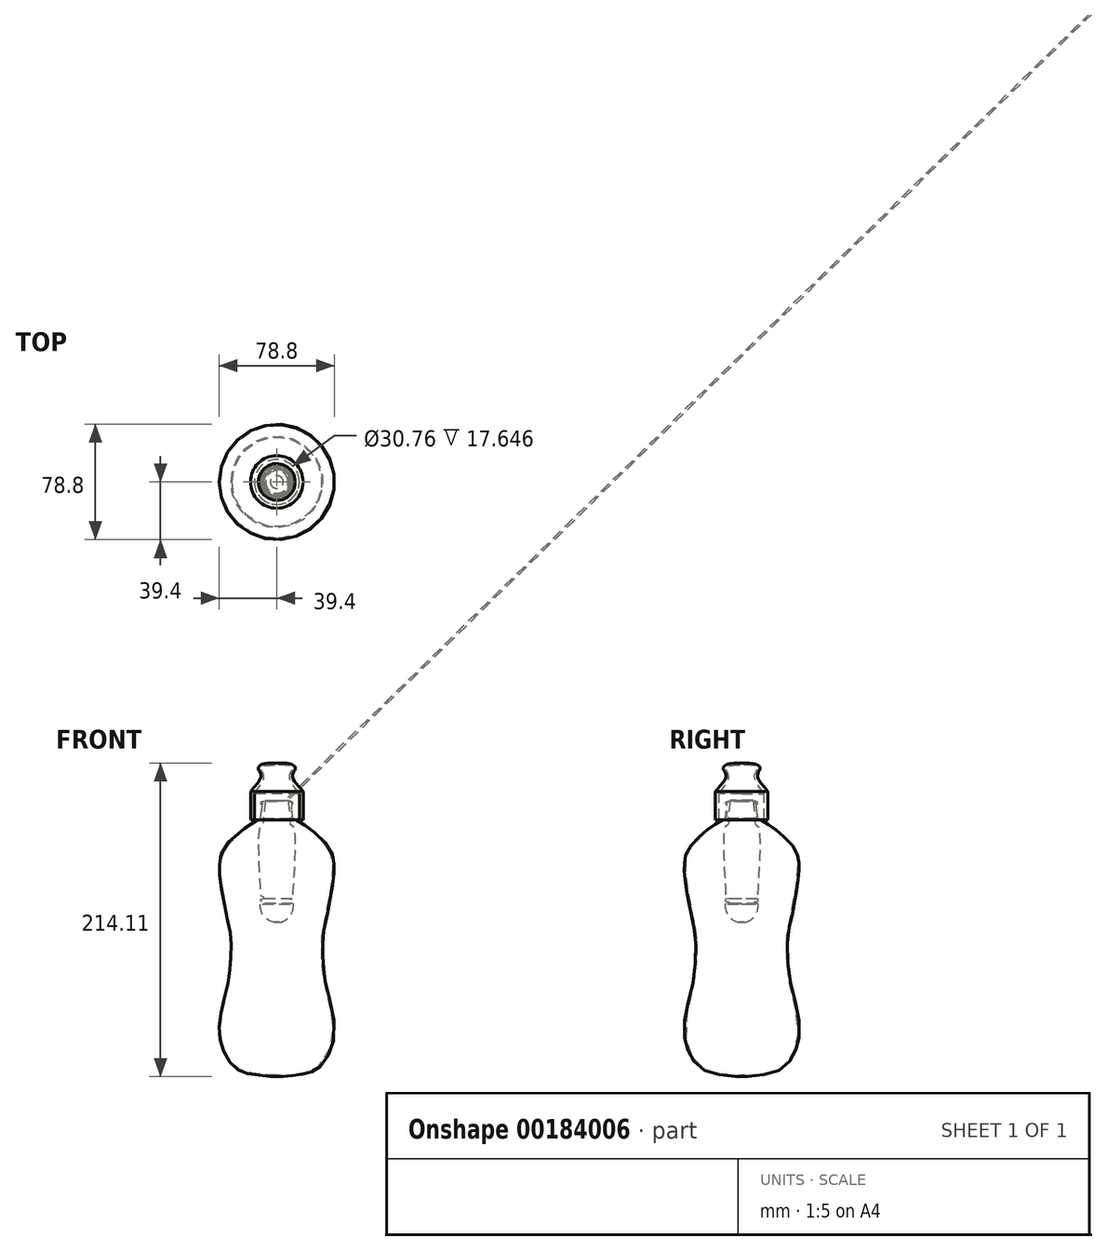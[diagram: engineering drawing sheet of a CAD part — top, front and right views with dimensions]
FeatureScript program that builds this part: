
annotation { "Feature Type Name" : "Feature", "Feature Type Description" : "" }
export const myFeature = defineFeature(function(context is Context, id is Id, definition is map)
    precondition{}
    {
        {
            var Q0;
            Q0=qCreatedBy(makeId("Front.planeOp"),FACE);
            var sketch = newSketch(context, id + "F0", { "sketchPlane" : qUnion([Q0])});
            skLineSegment(sketch, "E0", {"start": v(0, 125) * mm, "end": v(0, -125) * mm});
            skLineSegment(sketch, "E1", {"start": v(0, -112.64) * mm, "end": v(-4.36, -112.64) * mm});
            skFitSpline(sketch, "E2", {"points": [v(-4.36, -112.64) * mm, v(-16.45, -111.17) * mm, v(-26.5, -108.07) * mm, v(-34.94, -98.65) * mm, v(-39.23, -84.31) * mm, v(-37.9, -67.75) * mm, v(-33.02, -46.85) * mm, v(-31.39, -30.34) * mm, v(-31.69, -15.95) * mm, v(-34.64, -0.81) * mm, v(-38.74, 22.59) * mm, v(-39.11, 33.2) * mm, v(-33.62, 46.4) * mm, v(-11.97, 63.13) * mm, v(-11.2, 63.49) * mm, v(-10.64, 73.45) * mm, v(-11, 74.11) * mm, v(-10.27, 75) * mm, v(0, 75.52) * mm], "startDerivative": vector(-215.52, 22.72) * mm, "endDerivative": vector(247.21, -9.39) * mm});
            skFitSpline(sketch, "E3", {"points": [v(0, -111.79) * mm, v(-4.35, -111.82) * mm, v(-16.36, -110.37) * mm, v(-26.2, -107.54) * mm, v(-34.39, -98.27) * mm, v(-38.6, -84.25) * mm, v(-37.12, -67.8) * mm, v(-32.35, -46.82) * mm, v(-30.74, -30.3) * mm, v(-31.03, -15.9) * mm, v(-34.06, -0.62) * mm, v(-38, 22.72) * mm, v(-38.53, 33.18) * mm, v(-33.33, 46.15) * mm, v(-11.83, 62.8) * mm, v(-11.21, 62.9) * mm, v(-10.84, 63.44) * mm, v(-10.17, 67.96) * mm, v(-10.24, 73.55) * mm, v(-10.65, 74.13) * mm, v(-10.05, 74.78) * mm, v(0, 75.17) * mm], "startDerivative": vector(-115.99, -6.45) * mm, "endDerivative": vector(261.99, -8.08) * mm});
            skSolve(sketch);
        }
        {
            var Q0;
            Q0=qCreatedBy(makeId("Front.planeOp"),FACE);
            var sketch = newSketch(context, id + "F1", { "sketchPlane" : qUnion([Q0])});
            skFitSpline(sketch, "E4", {"points": [v(0, -7.07) * mm, v(-3.24, -7.07) * mm, v(-7.94, -4.31) * mm, v(-10.43, -0.72) * mm, v(-11.04, 5.37) * mm, v(-9.54, 5.26) * mm, v(-9.04, 6.64) * mm, v(-10.98, 7.03) * mm, v(-10.87, 8.47) * mm, v(-9.32, 8.63) * mm, v(-8.82, 9.74) * mm, v(-10.37, 10.13) * mm, v(-10.87, 10.68) * mm, v(-10.87, 11.62) * mm, v(-11.38, 57.7) * mm, v(-9.4, 59.38) * mm, v(-9.19, 61.78) * mm, v(-9.81, 62.2) * mm, v(-9.34, 63.6) * mm], "startDerivative": vector(-53.09, -8.54) * mm, "endDerivative": vector(23.68, 44.94) * mm});
            skLineSegment(sketch, "E5", {"start": v(0, -7.07) * mm, "end": v(0, 63.6) * mm});
            skLineSegment(sketch, "E6", {"start": v(0, 63.6) * mm, "end": v(-9.34, 63.6) * mm});
            skLineSegment(sketch, "E7", {"start": v(-9.34, 63.6) * mm, "end": v(-7.72, 75.84) * mm});
            skLineSegment(sketch, "E8", {"start": v(-7.72, 75.84) * mm, "end": v(0, 75.84) * mm});
            skLineSegment(sketch, "E9", {"start": v(0, 75.84) * mm, "end": v(0, 63.6) * mm});
            skSolve(sketch);
        }
        {
            var Q0;
            {var subQ1=sQuery(id+"F0.wireOp",EDGE,"E1");Q0=makeQuery(id+"F0.imprint","IMPRINT",FACE,{"disambiguationData":[TD([[makeQuery(id+"F0.imprint","IMPRINT",EDGE,{"derivedFrom":subQ1}),-1.0]])]});}
            var Q1;
            Q1=sQuery(id+"F0.wireOp",EDGE,"E0");
            revolve(context, id + "F2", {"entities" : qUnion([Q0]), "axis" : qUnion([Q1]), "revolveType" : RevolveType.FULL});
        }
        {
            var Q0;
            Q0=makeQuery(id+"F1.imprint","IMPRINT",FACE,{"disambiguationData":[TD([[makeQuery(id+"F1.imprint","IMPRINT",EDGE,{"derivedFrom":sQuery(id+"F1.wireOp",EDGE,"E4")}),-1.0]])]});
            var Q1;
            Q1=makeQuery(id+"F1.imprint","IMPRINT",FACE,{"disambiguationData":[TD([[makeQuery(id+"F1.imprint","IMPRINT",EDGE,{"derivedFrom":sQuery(id+"F1.wireOp",EDGE,"E6")}),-1.0]])]});
            var Q2;
            Q2=sQuery(id+"F1.wireOp",EDGE,"E5");
            revolve(context, id + "F3", {"entities" : qUnion([Q0, Q1]), "axis" : qUnion([Q2]), "revolveType" : RevolveType.FULL});
        }
        {
            var Q0;
            Q0=qCreatedBy(makeId("Front.planeOp"),FACE);
            var sketch = newSketch(context, id + "F4", { "sketchPlane" : qUnion([Q0])});
            skLineSegment(sketch, "E10", {"start": v(-15.38, 80.37) * mm, "end": v(-15.38, 62.73) * mm});
            skLineSegment(sketch, "E11", {"start": v(-15.38, 62.73) * mm, "end": v(-17.94, 62.73) * mm});
            skLineSegment(sketch, "E12", {"start": v(-17.94, 62.73) * mm, "end": v(-17.94, 82.05) * mm});
            skFitSpline(sketch, "E13", {"points": [v(-17.94, 82.05) * mm, v(-13.11, 87.76) * mm, v(-10.74, 92.3) * mm, v(-11.63, 95.45) * mm, v(-12.62, 97.92) * mm, v(-10.65, 100.28) * mm, v(0, 101.47) * mm], "startDerivative": vector(24.97, 28.24) * mm, "endDerivative": vector(51.47, 0.48) * mm});
            skFitSpline(sketch, "E14", {"points": [v(-15.38, 80.37) * mm, v(-11.14, 86.29) * mm, v(-8.77, 91.7) * mm, v(-10.15, 96.05) * mm, v(-11.14, 98.02) * mm, v(-9.86, 99.2) * mm, v(0, 99.99) * mm], "startDerivative": vector(21.39, 28.83) * mm, "endDerivative": vector(50, 0.54) * mm});
            skLineSegment(sketch, "E15", {"start": v(0, 101.47) * mm, "end": v(0, 99.99) * mm});
            skSolve(sketch);
        }
        {
            var Q0;
            Q0=makeQuery(id+"F4.imprint","IMPRINT",FACE,{"disambiguationData":[TD([[makeQuery(id+"F4.imprint","IMPRINT",EDGE,{"derivedFrom":sQuery(id+"F4.wireOp",EDGE,"E10")}),-1.0]])]});
            var Q1;
            Q1=sQuery(id+"F0.wireOp",EDGE,"E0");
            revolve(context, id + "F5", {"entities" : qUnion([Q0]), "axis" : qUnion([Q1]), "revolveType" : RevolveType.FULL});
        }
    });
